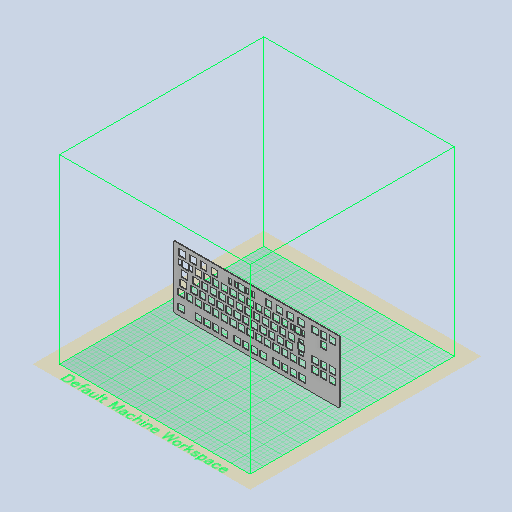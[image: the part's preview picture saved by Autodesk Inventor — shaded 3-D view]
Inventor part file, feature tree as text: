
AUTODESK INVENTOR PART (.ipt)
format: ipt  version: 2022 (Build 260153000, 153)  size: 4,683,264 bytes
history: native  units: mm
features: extrude x4, sketch x4, fillet x3, other x1, chamfer x1
ambient origin geometry x8: Origin, YZ Plane, XZ Plane, XY Plane, X Axis, Y Axis, Z Axis, Center Point
bodies: Body1 (feature_tree)
feature tree (13):
  other  "ソリッド1"
  extrude  "押し出し1"  Depth=3.0mm
  chamfer  "面取り1"  Distance=13.9954mm
  extrude  "押し出し2"  Depth=13.9954mm
  extrude  "押し出し3"  Depth=0.254mm
  fillet  "フィレット2"  Radius=19.05mm
  fillet  "フィレット3"  Radius=85.725mm
  extrude  "押し出し4"  Depth=54.61mm
  fillet  "フィレット4"  Radius=16.51mm
  sketch  "スケッチ1"
  sketch  "スケッチ2"
  sketch  "スケッチ3"
  sketch  "スケッチ4"
